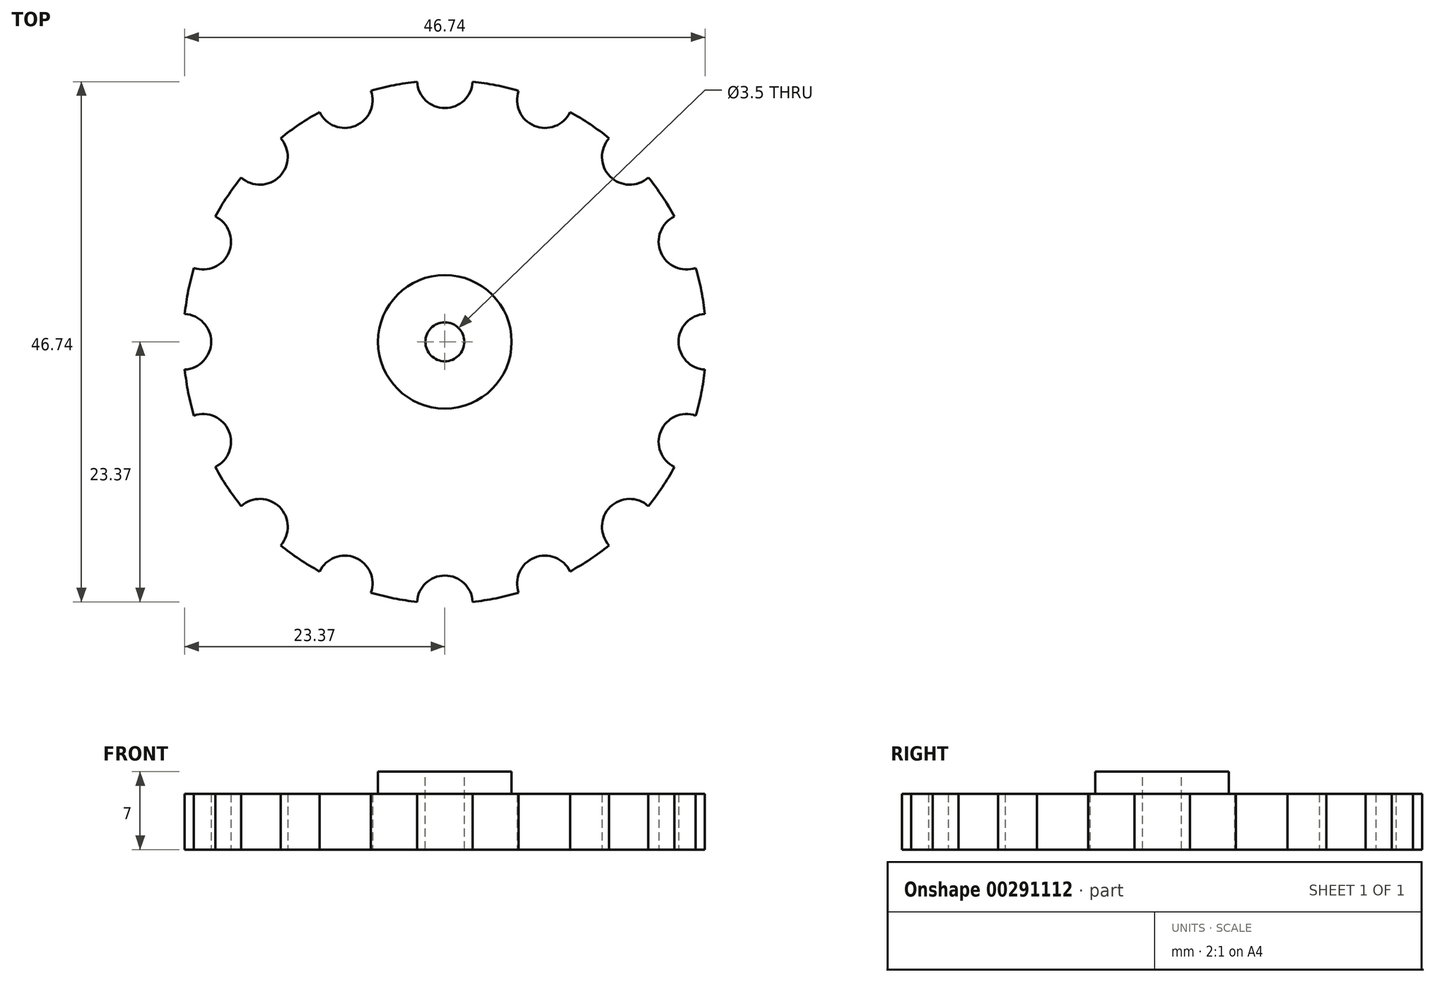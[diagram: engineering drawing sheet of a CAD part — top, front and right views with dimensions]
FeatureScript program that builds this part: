
annotation { "Feature Type Name" : "Feature", "Feature Type Description" : "" }
export const myFeature = defineFeature(function(context is Context, id is Id, definition is map)
    precondition{}
    {
        {
            var Q0;
            Q0=qCreatedBy(makeId("Top.planeOp"),FACE);
            var sketch = newSketch(context, id + "F0", { "sketchPlane" : qUnion([Q0])});
            skCircle(sketch, "E0", {"center": v(0, 0) * mm, "radius": 23.5 * mm});
            skCircle(sketch, "E1", {"center": v(0, 23.5) * mm, "radius": 2.5 * mm});
            skCircle(sketch, "E2.1.0", {"center": v(9, 21.71) * mm, "radius": 2.5 * mm});
            skCircle(sketch, "E2.2.0", {"center": v(16.62, 16.62) * mm, "radius": 2.5 * mm});
            skCircle(sketch, "E2.3.0", {"center": v(21.71, 9) * mm, "radius": 2.5 * mm});
            skCircle(sketch, "E2.4.0", {"center": v(23.5, 0) * mm, "radius": 2.5 * mm});
            skCircle(sketch, "E2.5.0", {"center": v(21.71, -9) * mm, "radius": 2.5 * mm});
            skCircle(sketch, "E2.6.0", {"center": v(16.62, -16.62) * mm, "radius": 2.5 * mm});
            skCircle(sketch, "E2.7.0", {"center": v(9, -21.71) * mm, "radius": 2.5 * mm});
            skCircle(sketch, "E2.8.0", {"center": v(0, -23.5) * mm, "radius": 2.5 * mm});
            skCircle(sketch, "E2.9.0", {"center": v(-9, -21.71) * mm, "radius": 2.5 * mm});
            skCircle(sketch, "E2.10.0", {"center": v(-16.62, -16.62) * mm, "radius": 2.5 * mm});
            skCircle(sketch, "E2.11.0", {"center": v(-21.71, -9) * mm, "radius": 2.5 * mm});
            skCircle(sketch, "E2.12.0", {"center": v(-23.5, 0) * mm, "radius": 2.5 * mm});
            skCircle(sketch, "E2.13.0", {"center": v(-21.71, 9) * mm, "radius": 2.5 * mm});
            skCircle(sketch, "E2.14.0", {"center": v(-16.62, 16.62) * mm, "radius": 2.5 * mm});
            skCircle(sketch, "E2.15.0", {"center": v(-9, 21.71) * mm, "radius": 2.5 * mm});
            skLineSegment(sketch, "E2.anchor1", {"start": v(0, 0) * mm, "end": v(0, 23.5) * mm, "construction": true});
            skLineSegment(sketch, "E2.anchor2", {"start": v(0, 0) * mm, "end": v(-9, 21.71) * mm, "construction": true});
            skSolve(sketch);
        }
        {
            var Q0;
            {var subQ1=sQuery(id+"F0.wireOp",EDGE,"E0");var subQ7=sQuery(id+"F0.wireOp",EDGE,"E2.3.0");var subQ8=makeQuery(id+"F0.imprint","INTERSECT",VERTEX,{"disambiguationData":[OD(0.0)],"derivedFrom":[subQ1,subQ7]});Q0=makeQuery(id+"F0.imprint","IMPRINT",FACE,{"disambiguationData":[TD([[makeQuery(id+"F0.imprint","IMPRINT",EDGE,{"disambiguationData":[TD([[subQ8,1.0]])],"derivedFrom":subQ1}),1.0]])]});}
            extrude(context, id + "F1", {"entities" : qUnion([Q0]), "depth" : 5 * mm});
        }
        {
            var Q0;
            Q0=makeQuery(id+"F1.opExtrude","CAP_FACE",FACE,{"disambiguationData":[OSD([sQuery(id+"F0.wireOp",EDGE,"E0"),sQuery(id+"F0.wireOp",EDGE,"E1"),sQuery(id+"F0.wireOp",EDGE,"E2.1.0"),sQuery(id+"F0.wireOp",EDGE,"E2.2.0"),sQuery(id+"F0.wireOp",EDGE,"E2.3.0"),sQuery(id+"F0.wireOp",EDGE,"E2.4.0"),sQuery(id+"F0.wireOp",EDGE,"E2.5.0"),sQuery(id+"F0.wireOp",EDGE,"E2.6.0"),sQuery(id+"F0.wireOp",EDGE,"E2.7.0"),sQuery(id+"F0.wireOp",EDGE,"E2.8.0"),sQuery(id+"F0.wireOp",EDGE,"E2.9.0"),sQuery(id+"F0.wireOp",EDGE,"E2.10.0"),sQuery(id+"F0.wireOp",EDGE,"E2.11.0"),sQuery(id+"F0.wireOp",EDGE,"E2.12.0"),sQuery(id+"F0.wireOp",EDGE,"E2.13.0"),sQuery(id+"F0.wireOp",EDGE,"E2.14.0"),sQuery(id+"F0.wireOp",EDGE,"E2.15.0")])],"isStart":false});
            var sketch = newSketch(context, id + "F2", { "sketchPlane" : qUnion([Q0])});
            skCircle(sketch, "E3", {"center": v(0, 0) * mm, "radius": 6 * mm});
            skSolve(sketch);
        }
        {
            var Q0;
            Q0 = qSketchRegion(id + "F2", true);
            extrude(context, id + "F3", {"entities" : qUnion([Q0]), "operationType" : NewBodyOperationType.ADD, "depth" : 2 * mm});
        }
        {
            var Q0;
            Q0=makeQuery(id+"F3.opExtrude","CAP_FACE",FACE,{"disambiguationData":[OSD([sQuery(id+"F2.wireOp",EDGE,"E3")])],"isStart":false});
            var sketch = newSketch(context, id + "F4", { "sketchPlane" : qUnion([Q0])});
            skCircle(sketch, "E4", {"center": v(0, 0) * mm, "radius": 1.75 * mm});
            skSolve(sketch);
        }
        {
            var Q0;
            Q0=makeQuery(id+"F4.imprint","IMPRINT",FACE,{"disambiguationData":[TD([[makeQuery(id+"F4.imprint","IMPRINT",EDGE,{"derivedFrom":sQuery(id+"F4.wireOp",EDGE,"E4")}),1.0]])]});
            extrude(context, id + "F5", {"entities" : qUnion([Q0]), "operationType" : NewBodyOperationType.REMOVE, "oppositeDirection" : true, "depth" : 25 * mm});
        }
    });
